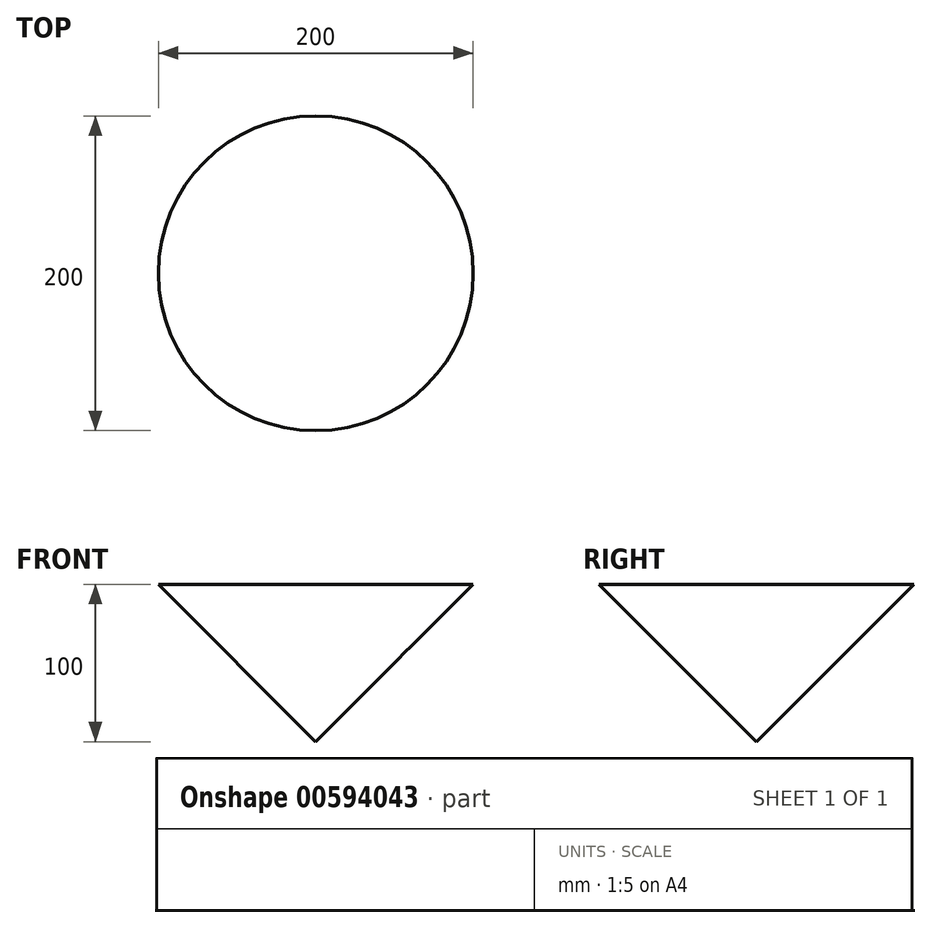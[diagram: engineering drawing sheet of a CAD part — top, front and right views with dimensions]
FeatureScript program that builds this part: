
annotation { "Feature Type Name" : "Feature", "Feature Type Description" : "" }
export const myFeature = defineFeature(function(context is Context, id is Id, definition is map)
    precondition{}
    {
        {
            var Q0;
            Q0=qCreatedBy(makeId("Front.planeOp"),FACE);
            var sketch = newSketch(context, id + "F0", { "sketchPlane" : qUnion([Q0])});
            skLineSegment(sketch, "E0", {"start": v(0, 0) * mm, "end": v(100, 100) * mm});
            skLineSegment(sketch, "E1", {"start": v(100, 100) * mm, "end": v(0, 100) * mm});
            skLineSegment(sketch, "E2", {"start": v(0, 100) * mm, "end": v(0, 0) * mm});
            skSolve(sketch);
        }
        {
            var Q0;
            Q0=qCreatedBy(makeId("Front.planeOp"),FACE);
            var sketch = newSketch(context, id + "F1", { "sketchPlane" : qUnion([Q0])});
            skLineSegment(sketch, "E3", {"start": v(0, 77.33) * mm, "end": v(0, -17.36) * mm, "construction": true});
            skSolve(sketch);
        }
        {
            var Q0;
            Q0 = qSketchRegion(id + "F0", true);
            var Q1;
            Q1=sQuery(id+"F1.wireOp",EDGE,"E3");
            revolve(context, id + "F2", {"entities" : qUnion([Q0]), "axis" : qUnion([Q1]), "revolveType" : RevolveType.FULL});
        }
    });
